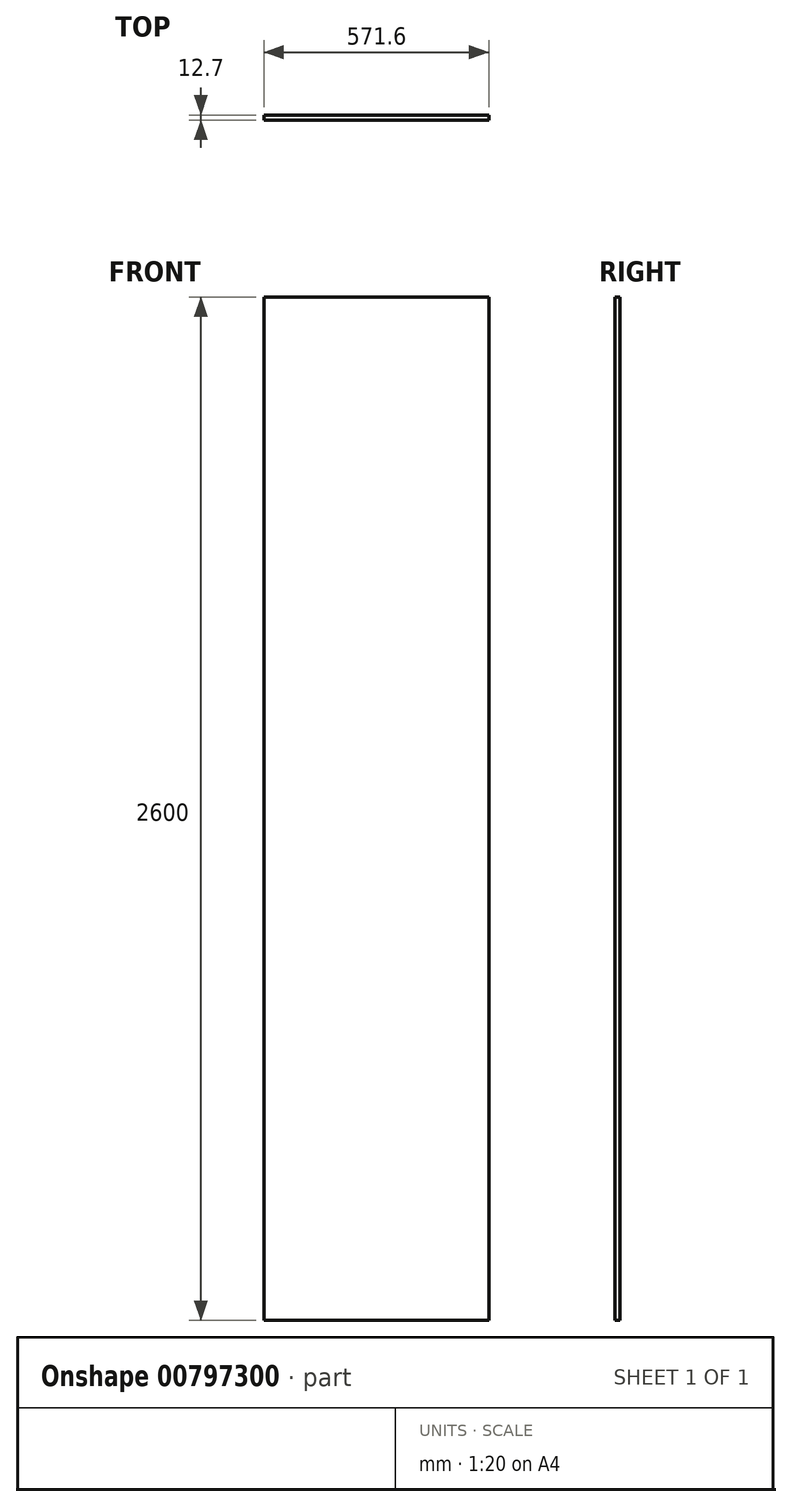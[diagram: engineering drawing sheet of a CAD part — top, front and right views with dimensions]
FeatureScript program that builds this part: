
annotation { "Feature Type Name" : "Feature", "Feature Type Description" : "" }
export const myFeature = defineFeature(function(context is Context, id is Id, definition is map)
    precondition{}
    {
        {
            var Q0;
            Q0=qCreatedBy(makeId("Front.planeOp"),FACE);
            var sketch = newSketch(context, id + "F0", { "sketchPlane" : qUnion([Q0])});
            skLineSegment(sketch, "E0.bottom", {"start": v(285.8, -1300) * mm, "end": v(-285.8, -1300) * mm});
            skLineSegment(sketch, "E0.top", {"start": v(285.8, 1300) * mm, "end": v(-285.8, 1300) * mm});
            skLineSegment(sketch, "E0.left", {"start": v(285.8, -1300) * mm, "end": v(285.8, 1300) * mm});
            skLineSegment(sketch, "E0.right", {"start": v(-285.8, -1300) * mm, "end": v(-285.8, 1300) * mm});
            skPoint(sketch, "E0.middle", {"position": v(0, 0) * mm});
            skSolve(sketch);
        }
        {
            var Q0;
            Q0=qSketchRegion(id+"F0",true);
            extrude(context, id + "F1", {"entities" : qUnion([Q0]), "depth" : (25.4 / 2) * mm, "offsetDistance" : 25 * mm, "symmetric" : true});
        }
    });
